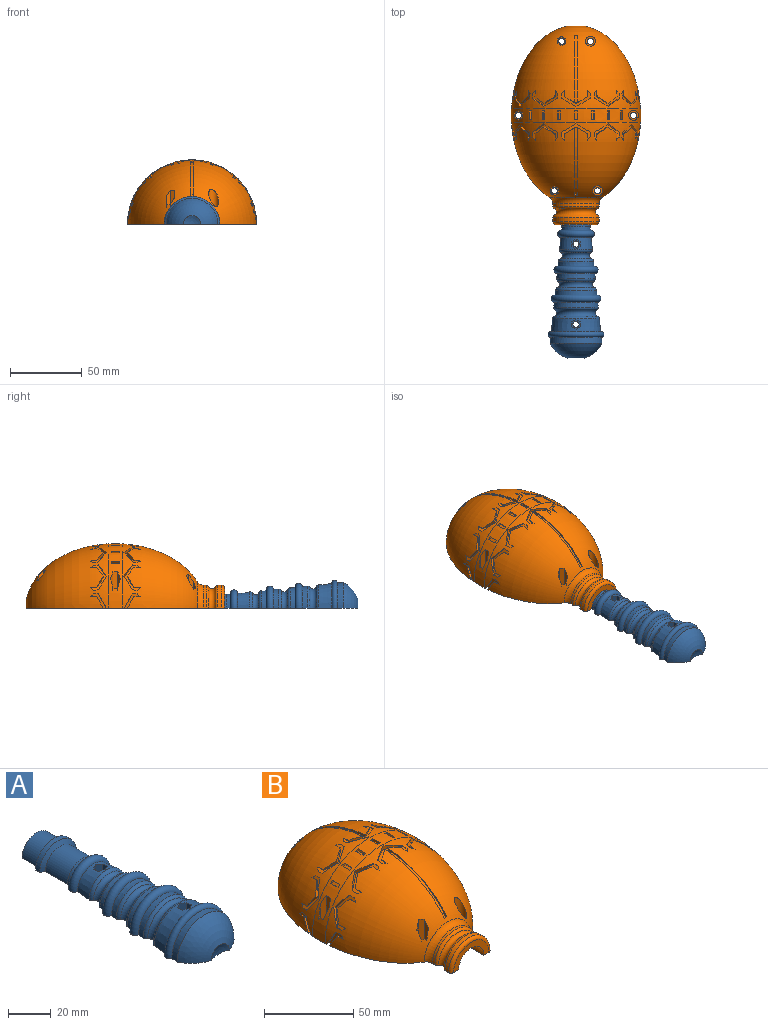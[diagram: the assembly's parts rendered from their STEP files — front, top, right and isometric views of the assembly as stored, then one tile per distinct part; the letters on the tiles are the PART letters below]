
ASSEMBLY  parts=2 mates=1
PART A: 46 faces, bbox 42x121.3x21 mm
  f0: cone r=16.12mm half-angle=5.8deg, axis (0,-1,0), area 445.7mm2, adj f13,f25,f26,f27,f28,f29,f30,f31
  f1: cone r=10.51mm half-angle=5.8deg, axis (0,-1,0), area 264mm2, adj f23,f25,f33,f34,f35,f36,f37,f38
  f2: cylinder r=2.12mm len=5mm, axis (0,0,-1), area 66.8mm2, adj f25,f39
  f3: cylinder r=2.12mm len=5mm, axis (0,0,-1), area 66.8mm2, adj f25,f32
  f4: cylinder r=9.75mm len=19.5mm, axis (0,1,0), area 445.9mm2, adj f5,f24,f25
  f5: cone r=9.75mm half-angle=60deg, axis (0,1,0), area 94.2mm2, adj f4,f6,f25
  f6: cylinder r=12.12mm len=24.25mm, axis (0,1,0), area 104.5mm2, adj f5,f7,f25
  f7: cone r=12.12mm half-angle=60deg, axis (0,-1,0), area 94.2mm2, adj f6,f8,f25
  f8: cylinder r=9.75mm len=19.5mm, axis (0,1,0), area 305mm2, adj f7,f9,f25
  f9: plane 19.5x9.75mm, normal (0,1,0), area 149.3mm2, adj f8,f25
  f10: sphere r=15mm, area 59mm2, adj f11,f25
  f11: sphere r=20mm, area 651mm2, adj f10,f12,f25
  f12: cone r=17.6mm half-angle=5.8deg, axis (0,-1,0), area 222.2mm2, adj f11,f13,f25
  f13: torus R=17.39mm, axis (0,1,0), area 368.3mm2, adj f0,f12,f25
  f14: torus R=15.86mm, axis (0,1,0), area 241.7mm2, adj f25,f40,f41
  f15: cone r=15.1mm half-angle=5.8deg, axis (0,-1,0), area 166.5mm2, adj f16,f25,f41
  f16: torus R=14.85mm, axis (0,1,0), area 405.5mm2, adj f15,f17,f25
  f17: cone r=14.08mm half-angle=5.8deg, axis (0,-1,0), area 159.5mm2, adj f16,f25,f42
  f18: torus R=13.83mm, axis (0,1,0), area 206.2mm2, adj f25,f42,f43
  f19: cone r=13.06mm half-angle=5.8deg, axis (0,-1,0), area 146.5mm2, adj f20,f25,f43
  f20: torus R=12.81mm, axis (0,1,0), area 355.1mm2, adj f19,f21,f25
  f21: cone r=12.04mm half-angle=5.8deg, axis (0,-1,0), area 136.9mm2, adj f20,f25,f44
  f22: torus R=11.79mm, axis (0,1,0), area 170.6mm2, adj f25,f44,f45
  f23: torus R=10.26mm, axis (0,1,0), area 292.2mm2, adj f1,f24,f25
  f24: cone r=9.75mm half-angle=5.8deg, axis (0,-1,0), area 78.4mm2, adj f4,f23,f25
  f25: plane 121.25x38.79mm, normal (0,0,-1), area 3102.5mm2, adj f0,f1,f2,f3,f4,f5,f6,f7
  f26: plane 12.03x2.93mm, normal (-0.5,0.87,0), area 39.9mm2, adj f0,f27,f31,f32
  f27: plane 11.59x3.37mm, normal (-1,0,0), area 38.5mm2, adj f0,f26,f28,f32
  f28: plane 11.37x2.93mm, normal (-0.5,-0.87,0), area 38.2mm2, adj f0,f27,f29,f32
  f29: plane 11.37x2.93mm, normal (0.5,-0.87,0), area 38.2mm2, adj f0,f28,f30,f32
  f30: plane 11.59x3.37mm, normal (1,0,0), area 38.5mm2, adj f0,f29,f31,f32
  f31: plane 12.03x2.93mm, normal (0.5,0.87,0), area 39.9mm2, adj f0,f26,f30,f32
  f32: plane 6.74x5.84mm, normal (0,0,1), area 15.3mm2, adj f3,f26,f27,f28,f29,f30,f31
  f33: plane 6.32x2.92mm, normal (-0.5,0.87,0), area 20.6mm2, adj f1,f34,f38,f39
  f34: plane 5.76x3.37mm, normal (-1,0,0), area 18.8mm2, adj f1,f33,f35,f39
  f35: plane 5.66x2.93mm, normal (-0.5,-0.87,0), area 18.8mm2, adj f1,f34,f36,f39
  f36: plane 5.66x2.93mm, normal (0.5,-0.87,0), area 18.8mm2, adj f1,f35,f37,f39
  f37: plane 5.76x3.37mm, normal (1,0,0), area 18.8mm2, adj f1,f36,f38,f39
  f38: plane 6.32x2.92mm, normal (0.5,0.87,0), area 20.6mm2, adj f1,f33,f37,f39
  f39: plane 6.74x5.84mm, normal (0,0,1), area 15.3mm2, adj f2,f33,f34,f35,f36,f37,f38
  f40: torus R=14.28mm, axis (0,-1,0), area 110.1mm2, adj f0,f14,f25
  f41: torus R=13.47mm, axis (0,-1,0), area 105.8mm2, adj f14,f15,f25
  f42: torus R=12.25mm, axis (0,-1,0), area 95.9mm2, adj f17,f18,f25
  f43: torus R=11.43mm, axis (0,-1,0), area 91.6mm2, adj f18,f19,f25
  f44: torus R=10.21mm, axis (0,-1,0), area 81.7mm2, adj f21,f22,f25
  f45: torus R=9.39mm, axis (0,-1,0), area 77.4mm2, adj f1,f22,f25
PART B: 213 faces, bbox 90.2x138.2x45.2 mm
  f0: revolved ~90x45mm, area 1172.9mm2, adj f1,f2,f5,f31,f32,f33,f34,f35
  f1: revolved ~89.71x52.06mm, area 6189.8mm2, adj f0,f5,f30,f38,f51,f52,f53,f54
  f2: revolved ~89.71x57.12mm, area 6751.5mm2, adj f0,f3,f4,f5,f20,f40,f41,f42
  f3: plane 8.04x4.66mm, normal (0.5,-0.87,0), area 12.9mm2, adj f2,f4,f64,f67,f175,f177
  f4: plane 8.04x4.66mm, normal (-0.5,-0.87,0), area 12.9mm2, adj f2,f3,f65,f67,f176,f177
  f5: plane 138.05x90mm, normal (0,0,-1), area 2406.3mm2, adj f0,f1,f2,f6,f7,f8,f9,f10
  f6: cylinder r=2.12mm len=5mm, axis (0,0,-1), area 66.8mm2, adj f5,f57
  f7: cylinder r=2.12mm len=5mm, axis (0,0,-1), area 66.8mm2, adj f5,f50
  f8: cylinder r=2.12mm len=5mm, axis (0,0,-1), area 66.8mm2, adj f5,f48
  f9: cylinder r=2.12mm len=5mm, axis (0,0,-1), area 66.8mm2, adj f5,f46
  f10: cylinder r=2.12mm len=5mm, axis (0,0,-1), area 66.8mm2, adj f5,f39
  f11: cylinder r=2.12mm len=5mm, axis (0,0,-1), area 66.8mm2, adj f5,f37
  f12: cone r=12.5mm half-angle=60deg, axis (0,-1,0), area 102mm2, adj f5,f13,f26
  f13: cylinder r=12.5mm len=25mm, axis (0,1,0), area 113.4mm2, adj f5,f12,f14
  f14: cone r=10mm half-angle=60deg, axis (0,1,0), area 102mm2, adj f5,f13,f15
  f15: cylinder r=10mm len=20mm, axis (0,1,0), area 403.7mm2, adj f5,f14,f16
  f16: plane 28x14mm, normal (0,-1,0), area 150.8mm2, adj f5,f15,f58
  f17: cylinder r=16mm len=32mm, axis (0,1,0), area 137.2mm2, adj f5,f58,f59
  f18: torus R=16mm, axis (0,1,0), area 243.9mm2, adj f5,f59,f60
  f19: cylinder r=16mm len=32mm, axis (0,1,0), area 92.4mm2, adj f5,f30,f60
  f20: sphere r=5mm, area 72.5mm2, adj f2,f5
  f21: plane 26.12x13.06mm, normal (0,-1,0), area 267.9mm2, adj f5,f27
  f22: revolved ~76.39x38.19mm, area 627.9mm2, adj f5,f27,f169
  f23: torus R=41mm, axis (0,1,0), area 868.4mm2, adj f5,f28,f169
  f24: revolved ~74.42x37.21mm, area 1202.8mm2, adj f5,f28,f29
  f25: plane 21.73x10.87mm, normal (0,1,0), area 28.4mm2, adj f5,f26,f29
  f26: cylinder r=10mm len=20mm, axis (0,1,0), area 308.3mm2, adj f5,f12,f25
  f27: torus R=13.06mm, axis (0,1,0), area 2551.3mm2, adj f5,f21,f22
  f28: torus R=13.47mm, axis (0,1,0), area 2518.9mm2, adj f5,f23,f24
  f29: torus R=10.87mm, axis (0,1,0), area 1976.4mm2, adj f5,f24,f25
  f30: torus R=21mm, axis (0,1,0), area 268.2mm2, adj f1,f5,f19
  f31: plane 15.65x3.09mm, normal (0.5,-0.87,0), area 41.3mm2, adj f0,f32,f36,f37
  f32: plane 8.64x3.48mm, normal (1,0,0), area 28.7mm2, adj f0,f31,f33,f37
  f33: plane 15.65x3.09mm, normal (0.5,0.87,0), area 41.3mm2, adj f0,f32,f34,f37
  f34: plane 20.56x3.01mm, normal (-0.5,0.87,0), area 61mm2, adj f0,f33,f35,f37
  f35: plane 20.55x3.43mm, normal (-1,0,0), area 69mm2, adj f0,f34,f36,f37
  f36: plane 20.56x3.01mm, normal (-0.5,-0.87,0), area 61mm2, adj f0,f31,f35,f37
  f37: plane 6.74x5.84mm, normal (0,0,1), area 15.3mm2, adj f11,f31,f32,f33,f34,f35,f36
  f38: cylinder r=3.5mm len=19.11mm, axis (0,0,-1), area 298mm2, adj f1,f39
  f39: plane 7x7mm, normal (0,0,1), area 24.3mm2, adj f10,f38
  f40: plane 21.94x2.95mm, normal (-0.5,0.87,0), area 72.8mm2, adj f2,f41,f45,f46
  f41: plane 21.34x3.47mm, normal (-1,0,0), area 65.6mm2, adj f2,f40,f42,f46
  f42: plane 17.69x3.05mm, normal (-0.5,-0.87,0), area 53.6mm2, adj f2,f41,f43,f46
  f43: plane 14.84x2.96mm, normal (0.5,-0.87,0), area 48.8mm2, adj f2,f42,f44,f46
  f44: plane 18.91x3.37mm, normal (1,0,0), area 57.1mm2, adj f2,f43,f45,f46
  f45: plane 21.99x3mm, normal (0.5,0.87,0), area 69mm2, adj f2,f40,f44,f46
  f46: plane 6.74x5.84mm, normal (0,0,1), area 15.3mm2, adj f9,f40,f41,f42,f43,f44,f45
  f47: cylinder r=3.5mm len=22.25mm, axis (0,0,-1), area 397mm2, adj f2,f48
  f48: plane 7x7mm, normal (0,0,1), area 24.3mm2, adj f8,f47
  f49: cylinder r=3.5mm len=21.32mm, axis (0,0,-1), area 324mm2, adj f0,f50
  f50: plane 7x7mm, normal (0,0,1), area 24.3mm2, adj f7,f49
  f51: plane 8.67x3mm, normal (0.5,0.87,0), area 28.8mm2, adj f1,f52,f56,f57
  f52: plane 13.9x2.92mm, normal (-0.5,0.87,0), area 38.4mm2, adj f1,f51,f53,f57
  f53: plane 18.25x3.37mm, normal (-1,0,0), area 54.5mm2, adj f1,f52,f54,f57
  f54: plane 18.46x2.95mm, normal (-0.5,-0.87,0), area 61.9mm2, adj f1,f53,f55,f57
  f55: plane 18.56x3.06mm, normal (0.5,-0.87,0), area 55.2mm2, adj f1,f54,f56,f57
  f56: plane 14.11x3.37mm, normal (1,0,0), area 38.7mm2, adj f1,f51,f55,f57
  f57: plane 6.74x5.84mm, normal (0,0,1), area 15.3mm2, adj f6,f51,f52,f53,f54,f55,f56
  f58: torus R=14mm, axis (0,1,0), area 150.7mm2, adj f5,f16,f17
  f59: torus R=14mm, axis (0,-1,0), area 108.9mm2, adj f5,f17,f18
  f60: torus R=14mm, axis (0,-1,0), area 108.9mm2, adj f5,f18,f19
  f61: plane 10.07x5.84mm, normal (-0.5,0.87,0), area 19mm2, adj f2,f62,f66,f67
  f62: plane 3.37x0.56mm, normal (-1,0,0), area 1mm2, adj f2,f61,f67
  f63: plane 3.37x0.56mm, normal (1,0,0), area 1mm2, adj f2,f66,f67
  f64: plane 4.36x0.81mm, normal (1,0,0), area 1.8mm2, adj f2,f3,f67
  f65: plane 4.36x0.81mm, normal (-1,0,0), area 1.8mm2, adj f2,f4,f67
  f66: plane 10.07x5.84mm, normal (0.5,0.87,0), area 19mm2, adj f2,f61,f63,f67
  f67: plane 20.13x11.41mm, normal (0,0,1), area 57.2mm2, adj f2,f3,f4,f61,f62,f63,f64,f65
  f68: plane 9.01x7.06mm, normal (-0.43,0.87,0.25), area 19mm2, adj f2,f69,f75,f76
  f69: plane 3.37x0.48mm, normal (-0.87,0,0.5), area 1mm2, adj f2,f68,f76
  f70: plane 3.37x0.48mm, normal (0.87,0,-0.5), area 1mm2, adj f2,f75,f76
  f71: plane 4.36x0.7mm, normal (0.87,0,-0.5), area 1.8mm2, adj f2,f72,f76
  f72: plane 7.37x5.87mm, normal (0.43,-0.87,-0.25), area 14.7mm2, adj f2,f71,f73,f76
  f73: plane 8.03x4.74mm, normal (-0.43,-0.87,0.25), area 14.7mm2, adj f2,f72,f74,f76
  f74: plane 4.36x0.7mm, normal (-0.87,0,0.5), area 1.8mm2, adj f2,f73,f76
  f75: plane 9.88x5.85mm, normal (0.43,0.87,-0.25), area 19mm2, adj f2,f68,f70,f76
  f76: plane 17.45x11.41mm, normal (0.5,0,0.87), area 57.2mm2, adj f2,f68,f69,f70,f71,f72,f73,f74
  f77: plane 9.88x5.85mm, normal (-0.25,0.87,0.43), area 19mm2, adj f2,f78,f84,f85
  f78: plane 3.37x0.48mm, normal (-0.5,0,0.87), area 1mm2, adj f2,f77,f85
  f79: plane 3.37x0.48mm, normal (0.5,0,-0.87), area 1mm2, adj f2,f84,f85
  f80: plane 4.36x0.7mm, normal (0.5,0,-0.87), area 1.8mm2, adj f2,f81,f85
  f81: plane 8.03x4.74mm, normal (0.25,-0.87,-0.43), area 14.7mm2, adj f2,f80,f82,f85
  f82: plane 7.37x5.87mm, normal (-0.25,-0.87,0.43), area 14.7mm2, adj f2,f81,f83,f85
  f83: plane 4.36x0.7mm, normal (-0.5,0,0.87), area 1.8mm2, adj f2,f82,f85
  f84: plane 9.01x7.06mm, normal (0.25,0.87,-0.43), area 19mm2, adj f2,f77,f79,f85
  f85: plane 17.45x11.41mm, normal (0.87,0,0.5), area 57.2mm2, adj f2,f77,f78,f79,f80,f81,f82,f83
  f86: plane 3.37x0.56mm, normal (0,0,-1), area 1mm2, adj f2,f89,f90
  f87: plane 4.36x0.81mm, normal (0,0,1), area 1.8mm2, adj f2,f88,f90
  f88: plane 8.04x4.66mm, normal (0,-0.87,0.5), area 14.7mm2, adj f2,f5,f87,f90
  f89: plane 10.07x5.84mm, normal (0,0.87,-0.5), area 19mm2, adj f2,f5,f86,f90
  f90: plane 11.41x10.13mm, normal (1,0,0), area 28.6mm2, adj f2,f5,f86,f87,f88,f89
  f91: plane 10.07x5.84mm, normal (0,0.87,-0.5), area 19mm2, adj f2,f5,f92,f95
  f92: plane 3.37x0.56mm, normal (0,0,-1), area 1mm2, adj f2,f91,f95
  f93: plane 4.36x0.81mm, normal (0,0,1), area 1.8mm2, adj f2,f94,f95
  f94: plane 8.04x4.66mm, normal (0,-0.87,0.5), area 14.7mm2, adj f2,f5,f93,f95
  f95: plane 11.41x10.13mm, normal (-1,0,0), area 28.6mm2, adj f2,f5,f91,f92,f93,f94
  f96: plane 9.01x7.06mm, normal (-0.25,0.87,-0.43), area 19mm2, adj f2,f97,f103,f104
  f97: plane 3.37x0.48mm, normal (-0.5,0,-0.87), area 1mm2, adj f2,f96,f104
  f98: plane 3.37x0.48mm, normal (0.5,0,0.87), area 1mm2, adj f2,f103,f104
  f99: plane 4.36x0.7mm, normal (0.5,0,0.87), area 1.8mm2, adj f2,f100,f104
  f100: plane 7.37x5.87mm, normal (0.25,-0.87,0.43), area 14.7mm2, adj f2,f99,f101,f104
  f101: plane 8.03x4.74mm, normal (-0.25,-0.87,-0.43), area 14.7mm2, adj f2,f100,f102,f104
  f102: plane 4.36x0.7mm, normal (-0.5,0,-0.87), area 1.8mm2, adj f2,f101,f104
  f103: plane 9.88x5.85mm, normal (0.25,0.87,0.43), area 19mm2, adj f2,f96,f98,f104
  f104: plane 17.45x11.41mm, normal (-0.87,0,0.5), area 57.2mm2, adj f2,f96,f97,f98,f99,f100,f101,f102
  f105: plane 9.88x5.85mm, normal (-0.43,0.87,-0.25), area 19mm2, adj f2,f106,f112,f113
  f106: plane 3.37x0.48mm, normal (-0.87,0,-0.5), area 1mm2, adj f2,f105,f113
  f107: plane 3.37x0.48mm, normal (0.87,0,0.5), area 1mm2, adj f2,f112,f113
  f108: plane 4.36x0.7mm, normal (0.87,0,0.5), area 1.8mm2, adj f2,f109,f113
  f109: plane 8.03x4.74mm, normal (0.43,-0.87,0.25), area 14.7mm2, adj f2,f108,f110,f113
  f110: plane 7.37x5.87mm, normal (-0.43,-0.87,-0.25), area 14.7mm2, adj f2,f109,f111,f113
  f111: plane 4.36x0.7mm, normal (-0.87,0,-0.5), area 1.8mm2, adj f2,f110,f113
  f112: plane 9.01x7.06mm, normal (0.43,0.87,0.25), area 19mm2, adj f2,f105,f107,f113
  f113: plane 17.45x11.41mm, normal (-0.5,0,0.87), area 57.2mm2, adj f2,f105,f106,f107,f108,f109,f110,f111
  f114: plane 10.07x5.84mm, normal (-0.5,-0.87,0), area 19mm2, adj f1,f115,f121,f122
  f115: plane 10.07x5.84mm, normal (0.5,-0.87,0), area 19mm2, adj f1,f114,f116,f122
  f116: plane 3.37x0.56mm, normal (1,0,0), area 1mm2, adj f1,f115,f122
  f117: plane 4.36x0.81mm, normal (1,0,0), area 1.8mm2, adj f1,f120,f122
  f118: plane 4.36x0.81mm, normal (-1,0,0), area 1.8mm2, adj f1,f119,f122
  f119: plane 8.04x4.66mm, normal (-0.5,0.87,0), area 12.9mm2, adj f1,f118,f120,f122,f171,f172
  f120: plane 8.04x4.66mm, normal (0.5,0.87,0), area 12.9mm2, adj f1,f117,f119,f122,f172,f173
  f121: plane 3.37x0.56mm, normal (-1,0,0), area 1mm2, adj f1,f114,f122
  f122: plane 20.13x11.41mm, normal (0,0,1), area 57.2mm2, adj f1,f114,f115,f116,f117,f118,f119,f120
  f123: plane 9.01x7.06mm, normal (-0.43,-0.87,0.25), area 19mm2, adj f1,f124,f130,f131
  f124: plane 9.88x5.85mm, normal (0.43,-0.87,-0.25), area 19mm2, adj f1,f123,f125,f131
  f125: plane 3.37x0.48mm, normal (0.87,0,-0.5), area 1mm2, adj f1,f124,f131
  f126: plane 4.36x0.7mm, normal (0.87,0,-0.5), area 1.8mm2, adj f1,f129,f131
  f127: plane 4.36x0.7mm, normal (-0.87,0,0.5), area 1.8mm2, adj f1,f128,f131
  f128: plane 8.03x4.74mm, normal (-0.43,0.87,0.25), area 14.7mm2, adj f1,f127,f129,f131
  f129: plane 7.37x5.87mm, normal (0.43,0.87,-0.25), area 14.7mm2, adj f1,f126,f128,f131
  f130: plane 3.37x0.48mm, normal (-0.87,0,0.5), area 1mm2, adj f1,f123,f131
  f131: plane 17.45x11.41mm, normal (0.5,0,0.87), area 57.2mm2, adj f1,f123,f124,f125,f126,f127,f128,f129
  f132: plane 9.88x5.85mm, normal (-0.25,-0.87,0.43), area 19mm2, adj f1,f133,f139,f140
  f133: plane 9.01x7.06mm, normal (0.25,-0.87,-0.43), area 19mm2, adj f1,f132,f134,f140
  f134: plane 3.37x0.48mm, normal (0.5,0,-0.87), area 1mm2, adj f1,f133,f140
  f135: plane 4.36x0.7mm, normal (0.5,0,-0.87), area 1.8mm2, adj f1,f138,f140
  f136: plane 4.36x0.7mm, normal (-0.5,0,0.87), area 1.8mm2, adj f1,f137,f140
  f137: plane 7.37x5.87mm, normal (-0.25,0.87,0.43), area 14.7mm2, adj f1,f136,f138,f140
  f138: plane 8.03x4.74mm, normal (0.25,0.87,-0.43), area 14.7mm2, adj f1,f135,f137,f140
  f139: plane 3.37x0.48mm, normal (-0.5,0,0.87), area 1mm2, adj f1,f132,f140
  f140: plane 17.45x11.41mm, normal (0.87,0,0.5), area 57.2mm2, adj f1,f132,f133,f134,f135,f136,f137,f138
  f141: plane 3.37x0.56mm, normal (0,0,-1), area 1mm2, adj f1,f143,f145
  f142: plane 4.36x0.81mm, normal (0,0,1), area 1.8mm2, adj f1,f144,f145
  f143: plane 10.07x5.84mm, normal (0,-0.87,-0.5), area 19mm2, adj f1,f5,f141,f145
  f144: plane 8.04x4.66mm, normal (0,0.87,0.5), area 14.7mm2, adj f1,f5,f142,f145
  f145: plane 11.41x10.13mm, normal (1,0,0), area 28.6mm2, adj f1,f5,f141,f142,f143,f144
  f146: plane 10.07x5.84mm, normal (0,-0.87,-0.5), area 19mm2, adj f1,f5,f149,f150
  f147: plane 4.36x0.81mm, normal (0,0,1), area 1.8mm2, adj f1,f148,f150
  f148: plane 8.04x4.66mm, normal (0,0.87,0.5), area 14.7mm2, adj f1,f5,f147,f150
  f149: plane 3.37x0.56mm, normal (0,0,-1), area 1mm2, adj f1,f146,f150
  f150: plane 11.41x10.13mm, normal (-1,0,0), area 28.6mm2, adj f1,f5,f146,f147,f148,f149
  f151: plane 9.01x7.06mm, normal (-0.25,-0.87,-0.43), area 19mm2, adj f1,f152,f158,f159
  f152: plane 9.88x5.85mm, normal (0.25,-0.87,0.43), area 19mm2, adj f1,f151,f153,f159
  f153: plane 3.37x0.48mm, normal (0.5,0,0.87), area 1mm2, adj f1,f152,f159
  f154: plane 4.36x0.7mm, normal (0.5,0,0.87), area 1.8mm2, adj f1,f157,f159
  f155: plane 4.36x0.7mm, normal (-0.5,0,-0.87), area 1.8mm2, adj f1,f156,f159
  f156: plane 8.03x4.74mm, normal (-0.25,0.87,-0.43), area 14.7mm2, adj f1,f155,f157,f159
  f157: plane 7.37x5.87mm, normal (0.25,0.87,0.43), area 14.7mm2, adj f1,f154,f156,f159
  f158: plane 3.37x0.48mm, normal (-0.5,0,-0.87), area 1mm2, adj f1,f151,f159
  f159: plane 17.45x11.41mm, normal (-0.87,0,0.5), area 57.2mm2, adj f1,f151,f152,f153,f154,f155,f156,f157
  f160: plane 9.88x5.85mm, normal (-0.43,-0.87,-0.25), area 19mm2, adj f1,f161,f167,f168
  f161: plane 9.01x7.06mm, normal (0.43,-0.87,0.25), area 19mm2, adj f1,f160,f162,f168
  f162: plane 3.37x0.48mm, normal (0.87,0,0.5), area 1mm2, adj f1,f161,f168
  f163: plane 4.36x0.7mm, normal (0.87,0,0.5), area 1.8mm2, adj f1,f166,f168
  f164: plane 4.36x0.7mm, normal (-0.87,0,-0.5), area 1.8mm2, adj f1,f165,f168
  f165: plane 7.37x5.87mm, normal (-0.43,0.87,-0.25), area 14.7mm2, adj f1,f164,f166,f168
  f166: plane 8.03x4.74mm, normal (0.43,0.87,0.25), area 14.7mm2, adj f1,f163,f165,f168
  f167: plane 3.37x0.48mm, normal (-0.87,0,-0.5), area 1mm2, adj f1,f160,f168
  f168: plane 17.45x11.41mm, normal (-0.5,0,0.87), area 57.2mm2, adj f1,f160,f161,f162,f163,f164,f165,f166
  f169: torus R=18.93mm, axis (0,1,0), area 2113.1mm2, adj f5,f22,f23
  f170: plane 2.03x0.62mm, normal (0,0.71,0.71), area 1.6mm2, adj f1,f171,f172,f173
  f171: plane 46.71x24.54mm, normal (1,0,0), area 47.9mm2, adj f1,f119,f170,f172
  f172: cylinder r=60mm len=46.69mm, axis (1,0,0), area 107.1mm2, adj f119,f120,f170,f171,f173
  f173: plane 46.71x24.54mm, normal (-1,0,0), area 47.9mm2, adj f1,f120,f170,f172
  f174: plane 2.03x0.62mm, normal (0,-0.71,0.71), area 1.6mm2, adj f2,f175,f176,f177
  f175: plane 46.71x24.54mm, normal (-1,0,0), area 47.9mm2, adj f2,f3,f174,f177
  f176: plane 46.71x24.54mm, normal (1,0,0), area 47.9mm2, adj f2,f4,f174,f177
  f177: cylinder r=60mm len=46.69mm, axis (1,0,0), area 107.1mm2, adj f3,f4,f174,f175,f176
  f178: plane 6.01x1.59mm, normal (-1,0,0), area 9.4mm2, adj f0,f179,f181,f182
  f179: plane 2x1.55mm, normal (0,-1,0), area 3.1mm2, adj f0,f178,f180,f182
  f180: plane 6.01x1.59mm, normal (1,0,0), area 9.4mm2, adj f0,f179,f181,f182
  f181: plane 2x1.55mm, normal (0,1,0), area 3.1mm2, adj f0,f178,f180,f182
  f182: plane 6x2mm, normal (0,0,1), area 12mm2, adj f178,f179,f180,f181
  f183: plane 6x1.13mm, normal (-0.71,0,-0.71), area 9.4mm2, adj f0,f184,f186,f187
  f184: plane 2.5x2.5mm, normal (0,-1,0), area 3.1mm2, adj f0,f183,f185,f187
  f185: plane 6x1.13mm, normal (0.71,0,0.71), area 9.4mm2, adj f0,f184,f186,f187
  f186: plane 2.5x2.5mm, normal (0,1,0), area 3.1mm2, adj f0,f183,f185,f187
  f187: plane 6x1.41mm, normal (-0.71,0,0.71), area 12mm2, adj f183,f184,f185,f186
  f188: plane 6x1.38mm, normal (-0.87,0,-0.5), area 9.4mm2, adj f0,f189,f191,f192
  f189: plane 2.5x2.33mm, normal (0,-1,0), area 3.1mm2, adj f0,f188,f190,f192
  f190: plane 6x1.38mm, normal (0.87,0,0.5), area 9.4mm2, adj f0,f189,f191,f192
  f191: plane 2.5x2.33mm, normal (0,1,0), area 3.1mm2, adj f0,f188,f190,f192
  f192: plane 6x1.73mm, normal (-0.5,0,0.87), area 12mm2, adj f188,f189,f190,f191
  f193: plane 6x1.54mm, normal (-0.97,0,-0.26), area 9.4mm2, adj f0,f194,f196,f197
  f194: plane 2.33x2mm, normal (0,-1,0), area 3.1mm2, adj f0,f193,f195,f197
  f195: plane 6x1.54mm, normal (0.97,0,0.26), area 9.4mm2, adj f0,f194,f196,f197
  f196: plane 2.33x2mm, normal (0,1,0), area 3.1mm2, adj f0,f193,f195,f197
  f197: plane 6x1.93mm, normal (-0.26,0,0.97), area 12mm2, adj f193,f194,f195,f196
  f198: plane 6x1.54mm, normal (-0.97,0,0.26), area 9.4mm2, adj f0,f199,f201,f202
  f199: plane 2.33x2mm, normal (0,-1,0), area 3.1mm2, adj f0,f198,f200,f202
  f200: plane 6x1.54mm, normal (0.97,0,-0.26), area 9.4mm2, adj f0,f199,f201,f202
  f201: plane 2.33x2mm, normal (0,1,0), area 3.1mm2, adj f0,f198,f200,f202
  f202: plane 6x1.93mm, normal (0.26,0,0.97), area 12mm2, adj f198,f199,f200,f201
  f203: plane 6x1.38mm, normal (-0.87,0,0.5), area 9.4mm2, adj f0,f204,f206,f207
  f204: plane 2.5x2.33mm, normal (0,-1,0), area 3.1mm2, adj f0,f203,f205,f207
  f205: plane 6x1.38mm, normal (0.87,0,-0.5), area 9.4mm2, adj f0,f204,f206,f207
  f206: plane 2.5x2.33mm, normal (0,1,0), area 3.1mm2, adj f0,f203,f205,f207
  f207: plane 6x1.73mm, normal (0.5,0,0.87), area 12mm2, adj f203,f204,f205,f206
  f208: plane 6x1.13mm, normal (-0.71,0,0.71), area 9.4mm2, adj f0,f209,f211,f212
  f209: plane 2.5x2.5mm, normal (0,-1,0), area 3.1mm2, adj f0,f208,f210,f212
  f210: plane 6x1.13mm, normal (0.71,0,-0.71), area 9.4mm2, adj f0,f209,f211,f212
  f211: plane 2.5x2.5mm, normal (0,1,0), area 3.1mm2, adj f0,f208,f210,f212
  f212: plane 6x1.41mm, normal (0.71,0,0.71), area 12mm2, adj f208,f209,f210,f211
PLACE A t=(-33.65,-69.93,5.42)mm
PLACE B t=(-33.65,7.57,5.42)mm
MATE cylindrical A.f24 <-> B.f12  axis (0,1,0) through (-33.65,-52.63,5.42)mm
